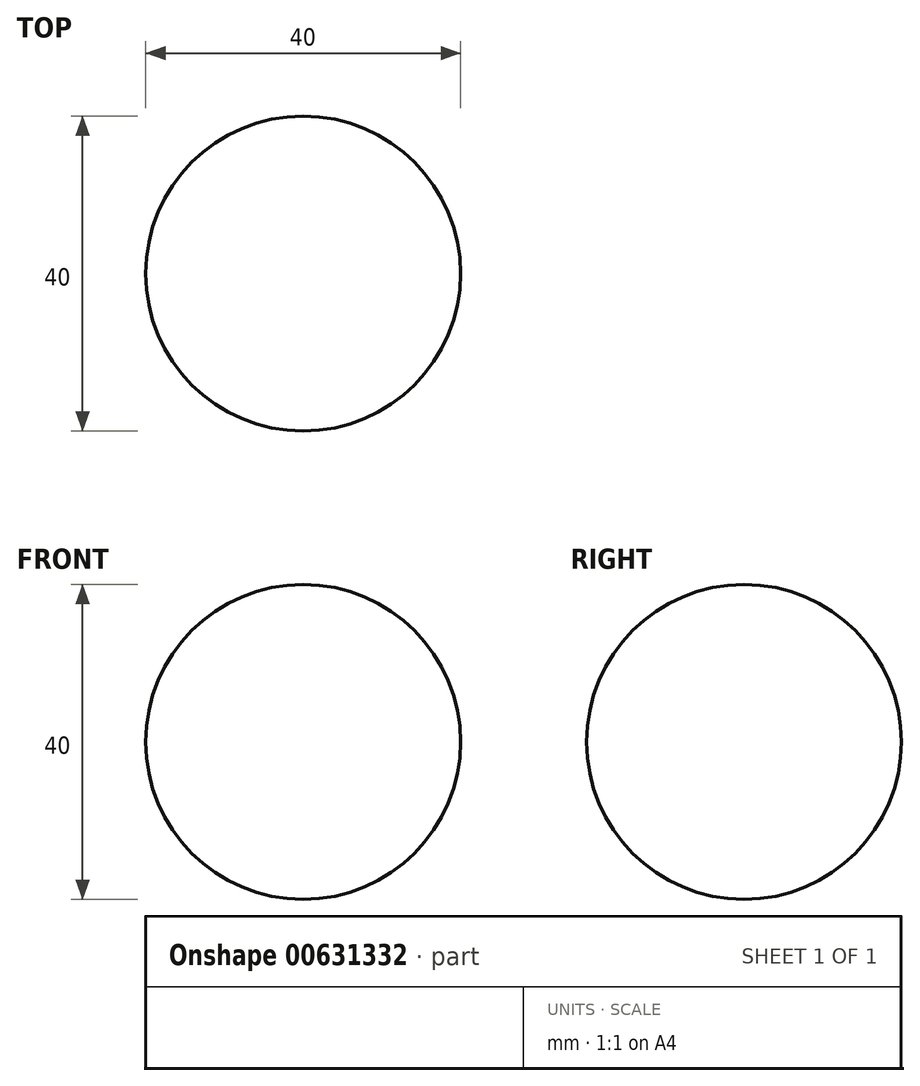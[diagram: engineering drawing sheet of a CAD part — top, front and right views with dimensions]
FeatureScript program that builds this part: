
annotation { "Feature Type Name" : "Feature", "Feature Type Description" : "" }
export const myFeature = defineFeature(function(context is Context, id is Id, definition is map)
    precondition{}
    {
        {
            var Q0;
            Q0=qCreatedBy(makeId("Front.planeOp"),FACE);
            var sketch = newSketch(context, id + "F0", { "sketchPlane" : qUnion([Q0])});
            skArc(sketch, "E0", {"start": v(0, -20) * mm, "mid": v(20, 0) * mm, "end": v(0, 20) * mm});
            skLineSegment(sketch, "E1", {"start": v(0, 20) * mm, "end": v(0, -20) * mm});
            skSolve(sketch);
        }
        {
            var Q0;
            Q0=makeQuery(id+"F0.imprint","IMPRINT",FACE,{"disambiguationData":[TD([[makeQuery(id+"F0.imprint","IMPRINT",EDGE,{"derivedFrom":sQuery(id+"F0.wireOp",EDGE,"E0")}),1.0]])]});
            var Q1;
            Q1=sQuery(id+"F0.wireOp",EDGE,"E1");
            revolve(context, id + "F1", {"entities" : qUnion([Q0]), "axis" : qUnion([Q1]), "revolveType" : RevolveType.FULL});
        }
    });
